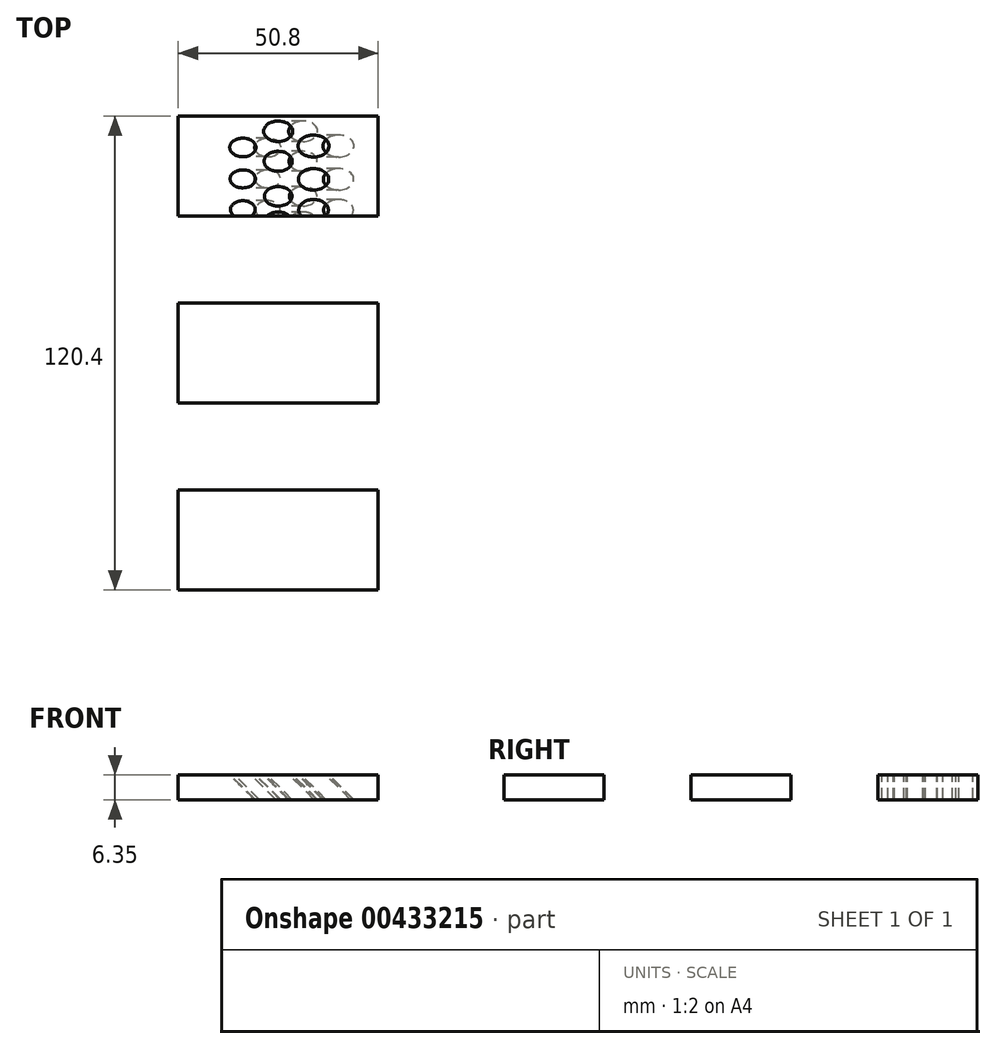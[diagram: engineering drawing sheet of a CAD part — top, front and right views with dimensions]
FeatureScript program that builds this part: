
annotation { "Feature Type Name" : "Feature", "Feature Type Description" : "" }
export const myFeature = defineFeature(function(context is Context, id is Id, definition is map)
    precondition{}
    {
        {
            var Q0;
            Q0=qCreatedBy(makeId("Top.planeOp"),FACE);
            var sketch = newSketch(context, id + "F0", { "sketchPlane" : qUnion([Q0])});
            skLineSegment(sketch, "E0.bottom", {"start": v(25.4, 12.7) * mm, "end": v(-25.4, 12.7) * mm});
            skLineSegment(sketch, "E0.top", {"start": v(25.4, -12.7) * mm, "end": v(-25.4, -12.7) * mm});
            skLineSegment(sketch, "E0.left", {"start": v(25.4, 12.7) * mm, "end": v(25.4, -12.7) * mm});
            skLineSegment(sketch, "E0.right", {"start": v(-25.4, 12.7) * mm, "end": v(-25.4, -12.7) * mm});
            skPoint(sketch, "E0.middle", {"position": v(0, 0) * mm});
            skLineSegment(sketch, "E1.bottom", {"start": v(-25.4, -34.8) * mm, "end": v(25.4, -34.8) * mm});
            skLineSegment(sketch, "E1.top", {"start": v(-25.4, -60.2) * mm, "end": v(25.4, -60.2) * mm});
            skLineSegment(sketch, "E1.left", {"start": v(-25.4, -34.8) * mm, "end": v(-25.4, -60.2) * mm});
            skLineSegment(sketch, "E1.right", {"start": v(25.4, -34.8) * mm, "end": v(25.4, -60.2) * mm});
            skLineSegment(sketch, "E2", {"start": v(-25.4, -34.8) * mm, "end": v(-25.4, -12.7) * mm, "construction": true});
            skLineSegment(sketch, "E3", {"start": v(-25.4, -60.2) * mm, "end": v(-25.4, -82.3) * mm, "construction": true});
            skLineSegment(sketch, "E4.bottom", {"start": v(-25.4, -82.3) * mm, "end": v(25.4, -82.3) * mm});
            skLineSegment(sketch, "E4.top", {"start": v(-25.4, -107.7) * mm, "end": v(25.4, -107.7) * mm});
            skLineSegment(sketch, "E4.left", {"start": v(-25.4, -82.3) * mm, "end": v(-25.4, -107.7) * mm});
            skLineSegment(sketch, "E4.right", {"start": v(25.4, -82.3) * mm, "end": v(25.4, -107.7) * mm});
            skSolve(sketch);
        }
        {
            var Q0;
            Q0 = qSketchRegion(id + "F0", true);
            extrude(context, id + "F1", {"entities" : qUnion([Q0]), "oppositeDirection" : true, "depth" : 6.35 * mm});
        }
        {
            var Q0;
            Q0=sQuery(id+"F0.wireOp",EDGE,"E0.right");
            cPlane(context, id + "F2", {"entities" : qUnion([Q0]), "cplaneType" : CPlaneType.LINE_ANGLE, "offset" : 25.4 * mm, "angle" : 45 * degree, "width" : 152.4 * mm, "height" : 152.4 * mm});
        }
        {
            var Q0;
            Q0=qCreatedBy(id+"F2.planeOp",FACE);
            var sketch = newSketch(context, id + "F3", { "sketchPlane" : qUnion([Q0])});
            skLineSegment(sketch, "E5.0", {"start": v(-22.45, 12.7) * mm, "end": v(-22.45, -12.7) * mm, "construction": true});
            skLineSegment(sketch, "E6", {"start": v(-22.45, 0) * mm, "end": v(40.1, 0) * mm, "construction": true});
            skCircle(sketch, "E7", {"center": v(-14.09, 0) * mm, "radius": 2.41 * mm});
            skCircle(sketch, "E8", {"center": v(-7.7, 0) * mm, "radius": 2.48 * mm});
            skCircle(sketch, "E9", {"center": v(1.2, 0) * mm, "radius": 2.54 * mm});
            skCircle(sketch, "E10", {"center": v(8.82, 0) * mm, "radius": 2.6 * mm});
            skLineSegment(sketch, "E11", {"start": v(-22.45, 0) * mm, "end": v(-26.4, 0) * mm, "construction": true});
            skLineSegment(sketch, "E12", {"start": v(-26.4, 0) * mm, "end": v(-26.4, -12.7) * mm, "construction": true});
            skLineSegment(sketch, "E13", {"start": v(-26.4, -12.7) * mm, "end": v(-22.45, -12.7) * mm, "construction": true});
            skLineSegment(sketch, "E14", {"start": v(-26.4, -6.35) * mm, "end": v(38.83, -6.35) * mm, "construction": true});
            skCircle(sketch, "E15", {"center": v(-11.05, -6.35) * mm, "radius": 2.22 * mm});
            skCircle(sketch, "E16", {"center": v(-3.26, -6.35) * mm, "radius": 2.29 * mm});
            skCircle(sketch, "E17", {"center": v(4.72, -6.35) * mm, "radius": 2.35 * mm});
            skLineSegment(sketch, "E18", {"start": v(-22.45, 12.7) * mm, "end": v(-26.4, 12.7) * mm});
            skLineSegment(sketch, "E19", {"start": v(-26.4, 12.7) * mm, "end": v(-26.4, 0) * mm, "construction": true});
            skLineSegment(sketch, "E20", {"start": v(-26.4, 6.35) * mm, "end": v(39.02, 6.35) * mm});
            skCircle(sketch, "E21", {"center": v(-11.18, 6.35) * mm, "radius": 2.67 * mm});
            skCircle(sketch, "E22", {"center": v(-3.38, 6.35) * mm, "radius": 2.73 * mm});
            skCircle(sketch, "E23", {"center": v(5.07, 6.35) * mm, "radius": 2.8 * mm});
            skPoint(sketch, "E24.0", {"position": v(13.47, 12.7) * mm});
            skLineSegment(sketch, "E24.1", {"start": v(13.47, -12.7) * mm, "end": v(13.47, 12.7) * mm, "construction": true});
            skLineSegment(sketch, "E25.0", {"start": v(-17.96, -12.7) * mm, "end": v(-17.96, 12.7) * mm, "construction": true});
            skLineSegment(sketch, "E26.0", {"start": v(-17.96, 34.8) * mm, "end": v(-17.96, 60.2) * mm, "construction": true});
            skLineSegment(sketch, "E27.0", {"start": v(13.47, 34.8) * mm, "end": v(13.47, 60.2) * mm, "construction": true});
            skLineSegment(sketch, "E28", {"start": v(43.62, 34.8) * mm, "end": v(-17.96, 34.8) * mm, "construction": true});
            skLineSegment(sketch, "E29", {"start": v(43.62, 34.8) * mm, "end": v(43.62, 47.5) * mm, "construction": true});
            skLineSegment(sketch, "E30", {"start": v(-17.96, 47.5) * mm, "end": v(43.62, 47.5) * mm, "construction": true});
            skLineSegment(sketch, "E31", {"start": v(43.62, 47.5) * mm, "end": v(43.62, 60.2) * mm, "construction": true});
            skLineSegment(sketch, "E32", {"start": v(-17.96, 60.2) * mm, "end": v(43.62, 60.2) * mm, "construction": true});
            skLineSegment(sketch, "E33", {"start": v(43.62, 41.15) * mm, "end": v(-17.96, 41.15) * mm, "construction": true});
            skLineSegment(sketch, "E34", {"start": v(43.62, 53.85) * mm, "end": v(-17.96, 53.85) * mm, "construction": true});
            skCircle(sketch, "E35", {"center": v(-10.06, 41.15) * mm, "radius": 1.46 * mm});
            skCircle(sketch, "E36", {"center": v(-3.25, 41.15) * mm, "radius": 1.52 * mm});
            skCircle(sketch, "E37", {"center": v(4.07, 41.15) * mm, "radius": 1.59 * mm});
            skCircle(sketch, "E38", {"center": v(-14.33, 47.5) * mm, "radius": 1.65 * mm});
            skCircle(sketch, "E39", {"center": v(-7.63, 47.5) * mm, "radius": 1.71 * mm});
            skCircle(sketch, "E40", {"center": v(-0.42, 47.5) * mm, "radius": 1.78 * mm});
            skCircle(sketch, "E41", {"center": v(8.5, 47.5) * mm, "radius": 1.84 * mm});
            skCircle(sketch, "E42", {"center": v(-10.69, 53.85) * mm, "radius": 1.9 * mm});
            skCircle(sketch, "E43", {"center": v(-2.93, 53.85) * mm, "radius": 1.97 * mm});
            skCircle(sketch, "E44", {"center": v(5.74, 53.85) * mm, "radius": 2.03 * mm});
            skLineSegment(sketch, "E45.0", {"start": v(-17.96, 82.3) * mm, "end": v(-17.96, 107.7) * mm, "construction": true});
            skLineSegment(sketch, "E46.0", {"start": v(13.47, 82.3) * mm, "end": v(13.47, 107.7) * mm, "construction": true});
            skLineSegment(sketch, "E47", {"start": v(-17.96, 95) * mm, "end": v(-17.96, 95) * mm});
            skPoint(sketch, "E47.endSnap0", {"position": v(13.47, 95) * mm});
            skLineSegment(sketch, "E48", {"start": v(-17.96, 95) * mm, "end": v(-17.96, 82.3) * mm, "construction": true});
            skLineSegment(sketch, "E49", {"start": v(-17.96, 82.3) * mm, "end": v(-17.96, 82.3) * mm});
            skLineSegment(sketch, "E50", {"start": v(-17.96, 88.65) * mm, "end": v(-17.96, 88.65) * mm});
            skLineSegment(sketch, "E51", {"start": v(-17.96, 95) * mm, "end": v(-17.96, 107.7) * mm, "construction": true});
            skLineSegment(sketch, "E52", {"start": v(-17.96, 107.7) * mm, "end": v(-17.96, 107.7) * mm});
            skLineSegment(sketch, "E53", {"start": v(-17.96, 101.35) * mm, "end": v(-17.96, 101.35) * mm});
            skCircle(sketch, "E54", {"center": v(-13.28, 88.65) * mm, "radius": 2.86 * mm});
            skCircle(sketch, "E55", {"center": v(-6.15, 88.65) * mm, "radius": 2.92 * mm});
            skCircle(sketch, "E56", {"center": v(1.35, 88.65) * mm, "radius": 2.98 * mm});
            skCircle(sketch, "E57", {"center": v(9.25, 88.65) * mm, "radius": 3.05 * mm});
            skCircle(sketch, "E58", {"center": v(-10.01, 95) * mm, "radius": 3.11 * mm});
            skCircle(sketch, "E59", {"center": v(-2.72, 95) * mm, "radius": 3.18 * mm});
            skCircle(sketch, "E60", {"center": v(5.08, 95) * mm, "radius": 3.24 * mm});
            skCircle(sketch, "E61", {"center": v(-13.7, 101.35) * mm, "radius": 3.3 * mm});
            skCircle(sketch, "E62", {"center": v(-6.35, 101.35) * mm, "radius": 3.37 * mm});
            skCircle(sketch, "E63", {"center": v(1.25, 101.35) * mm, "radius": 3.43 * mm});
            skLineSegment(sketch, "E64", {"start": v(-17.96, 107.7) * mm, "end": v(33.8, 107.7) * mm, "construction": true});
            skLineSegment(sketch, "E65", {"start": v(33.8, 107.7) * mm, "end": v(33.8, 95) * mm, "construction": true});
            skLineSegment(sketch, "E66", {"start": v(33.8, 95) * mm, "end": v(33.8, 82.3) * mm, "construction": true});
            skLineSegment(sketch, "E67", {"start": v(33.8, 82.3) * mm, "end": v(-17.96, 82.3) * mm, "construction": true});
            skLineSegment(sketch, "E68", {"start": v(33.8, 88.65) * mm, "end": v(-17.96, 88.65) * mm, "construction": true});
            skLineSegment(sketch, "E69", {"start": v(33.8, 101.35) * mm, "end": v(-17.96, 101.35) * mm, "construction": true});
            skLineSegment(sketch, "E70", {"start": v(33.8, 95) * mm, "end": v(-17.96, 95) * mm, "construction": true});
            skPoint(sketch, "E71", {"position": v(7.92, 95) * mm});
            skCircle(sketch, "E72", {"center": v(9.12, 101.35) * mm, "radius": 3.5 * mm});
            skSolve(sketch);
        }
        {
            var Q0;
            Q0 = qSketchRegion(id + "F3", true);
            extrude(context, id + "F4", {"entities" : qUnion([Q0]), "operationType" : NewBodyOperationType.REMOVE, "endBound" : BoundingType.THROUGH_ALL, "depth" : 25.4 * mm});
        }
    });
